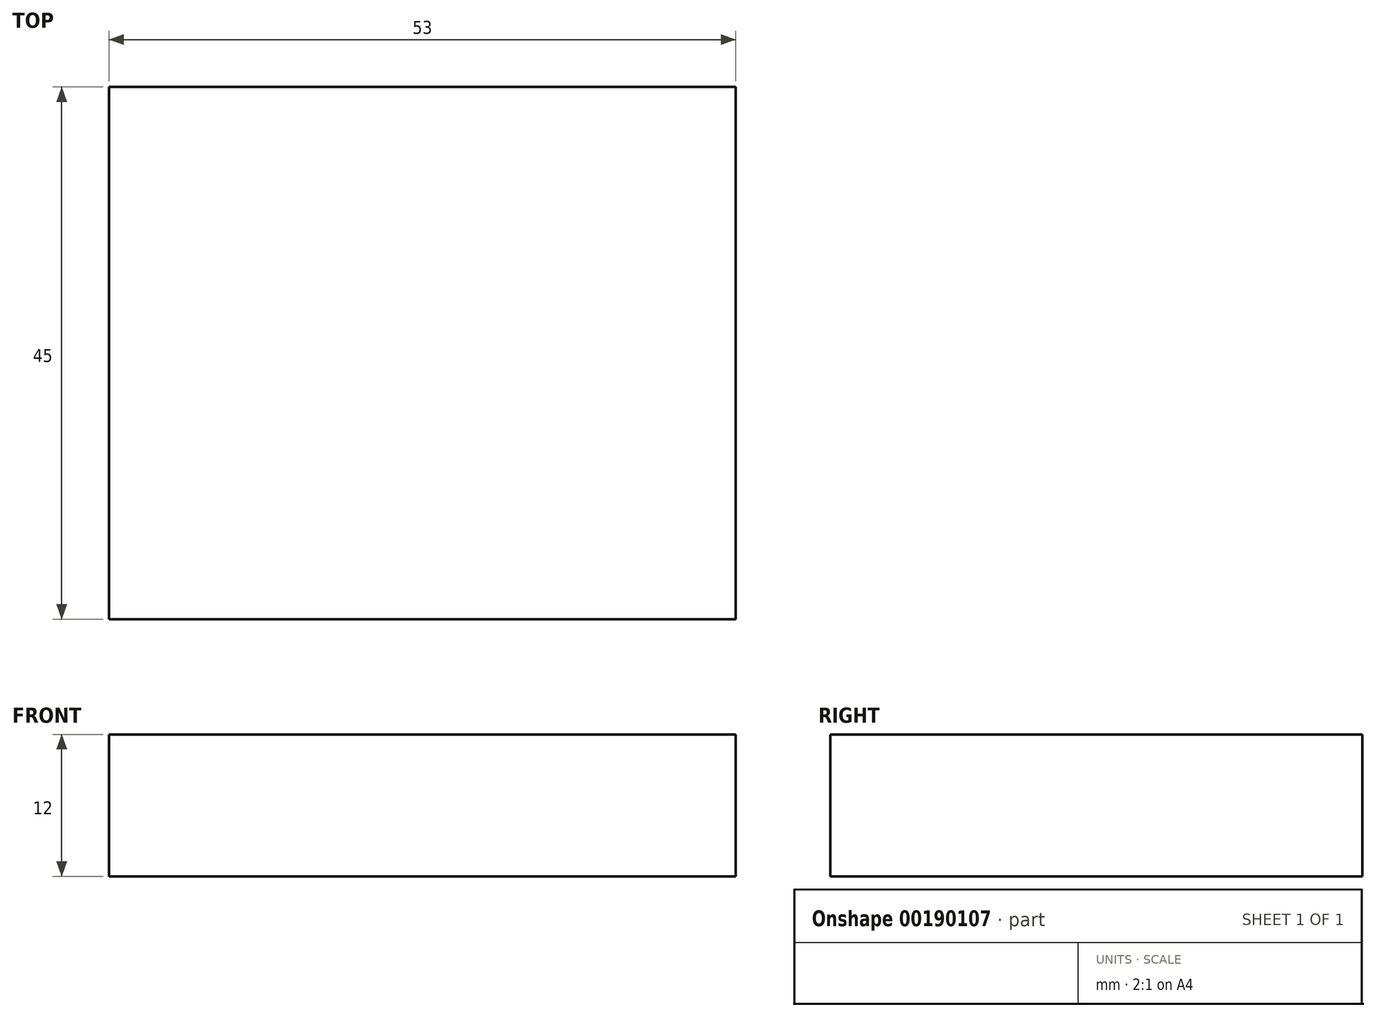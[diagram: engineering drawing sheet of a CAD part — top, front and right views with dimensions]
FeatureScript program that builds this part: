
annotation { "Feature Type Name" : "Feature", "Feature Type Description" : "" }
export const myFeature = defineFeature(function(context is Context, id is Id, definition is map)
    precondition{}
    {
        {
            var Q0;
            Q0=qCreatedBy(makeId("Top.planeOp"),FACE);
            var sketch = newSketch(context, id + "F0", { "sketchPlane" : qUnion([Q0])});
            skLineSegment(sketch, "E0.bottom", {"start": v(-26.5, -22.5) * mm, "end": v(26.5, -22.5) * mm});
            skLineSegment(sketch, "E0.top", {"start": v(-26.5, 22.5) * mm, "end": v(26.5, 22.5) * mm});
            skLineSegment(sketch, "E0.left", {"start": v(-26.5, -22.5) * mm, "end": v(-26.5, 22.5) * mm});
            skLineSegment(sketch, "E0.right", {"start": v(26.5, -22.5) * mm, "end": v(26.5, 22.5) * mm});
            skPoint(sketch, "E0.middle", {"position": v(0, 0) * mm});
            skSolve(sketch);
        }
        {
            var Q0;
            Q0=makeQuery(id+"F0.imprint","IMPRINT",FACE,{"disambiguationData":[TD([[makeQuery(id+"F0.imprint","IMPRINT",EDGE,{"derivedFrom":sQuery(id+"F0.wireOp",EDGE,"E0.bottom")}),1.0]])]});
            extrude(context, id + "F1", {"entities" : qUnion([Q0]), "depth" : 12 * mm});
        }
    });
